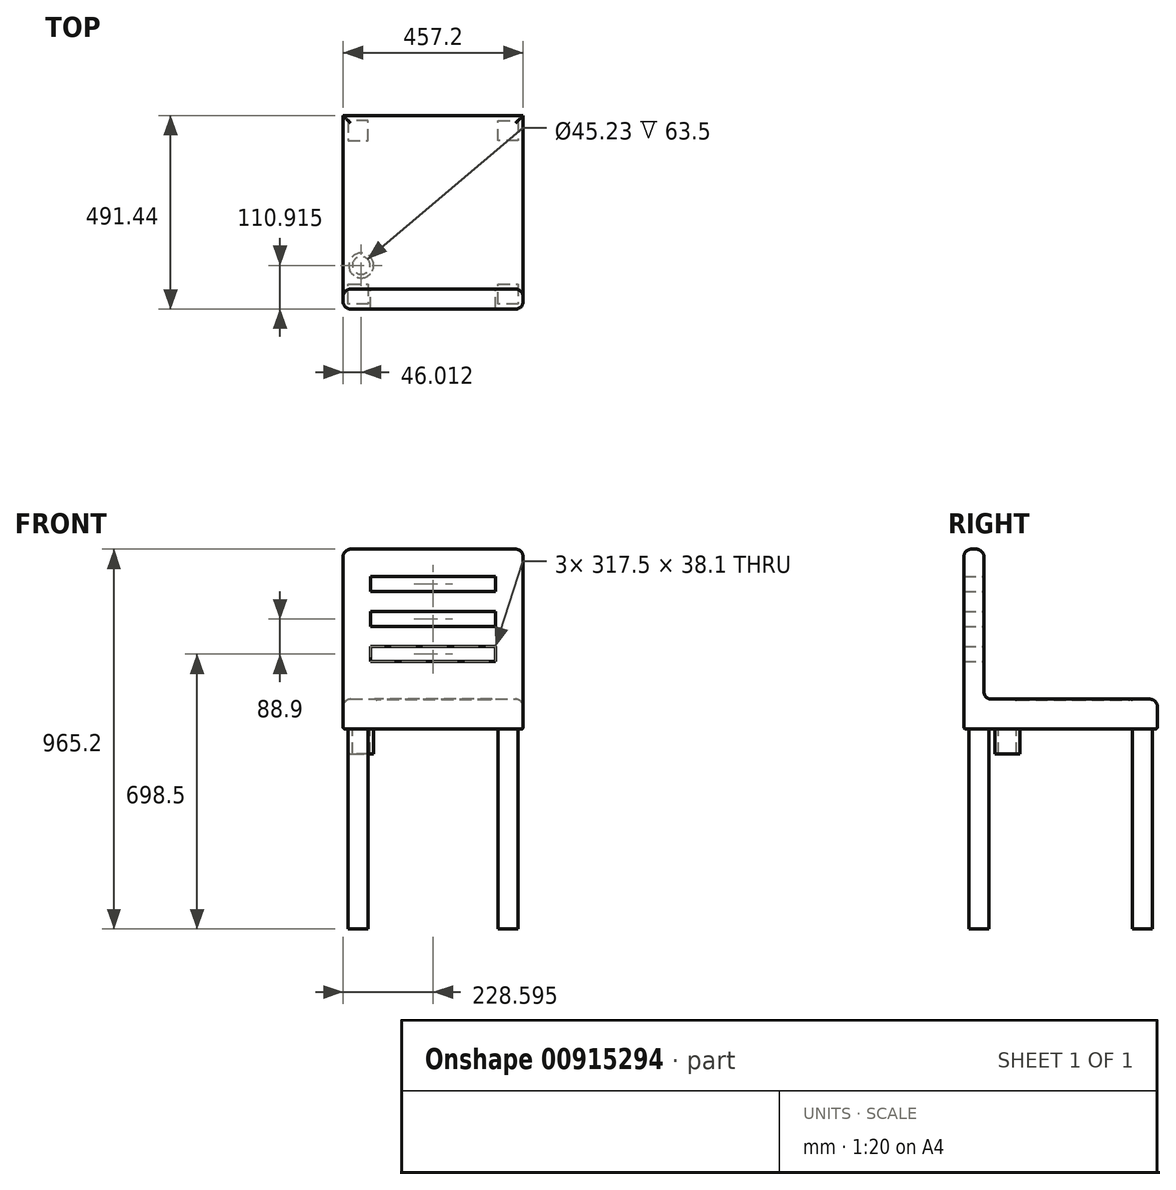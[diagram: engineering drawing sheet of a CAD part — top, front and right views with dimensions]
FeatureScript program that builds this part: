
annotation { "Feature Type Name" : "Feature", "Feature Type Description" : "" }
export const myFeature = defineFeature(function(context is Context, id is Id, definition is map)
    precondition{}
    {
        {
            var Q0;
            Q0=qCreatedBy(makeId("Top.planeOp"),FACE);
            var sketch = newSketch(context, id + "F0", { "sketchPlane" : qUnion([Q0])});
            skLineSegment(sketch, "E0.bottom", {"start": v(-229.23, 212.04) * mm, "end": v(227.97, 212.04) * mm});
            skLineSegment(sketch, "E0.top", {"start": v(-229.23, -245.16) * mm, "end": v(227.97, -245.16) * mm});
            skLineSegment(sketch, "E0.left", {"start": v(-229.23, 212.04) * mm, "end": v(-229.23, -245.16) * mm});
            skLineSegment(sketch, "E0.right", {"start": v(227.97, 212.04) * mm, "end": v(227.97, -245.16) * mm});
            skSolve(sketch);
        }
        {
            var Q0;
            Q0=qCreatedBy(makeId("Front.planeOp"),FACE);
            cPlane(context, id + "F1", {"entities" : qUnion([Q0]), "cplaneType" : CPlaneType.OFFSET, "offset" : 228.6 * mm, "width" : 152.4 * mm, "height" : 152.4 * mm});
        }
        {
            var Q0;
            Q0=qCreatedBy(id+"F1.planeOp",FACE);
            var sketch = newSketch(context, id + "F2", { "sketchPlane" : qUnion([Q0])});
            skLineSegment(sketch, "E1", {"start": v(-229.23, 0) * mm, "end": v(-229.23, 457.2) * mm});
            skLineSegment(sketch, "E2", {"start": v(-229.23, 457.2) * mm, "end": v(227.97, 457.2) * mm});
            skLineSegment(sketch, "E3", {"start": v(227.97, 457.2) * mm, "end": v(227.97, 0) * mm});
            skLineSegment(sketch, "E4", {"start": v(-229.23, 0) * mm, "end": v(227.97, 0) * mm});
            skSolve(sketch);
        }
        {
            var Q0;
            Q0=makeQuery(id+"F2.imprint","IMPRINT",FACE,{"disambiguationData":[TD([[makeQuery(id+"F2.imprint","IMPRINT",EDGE,{"derivedFrom":sQuery(id+"F2.wireOp",EDGE,"E1")}),-1.0]])]});
            extrude(context, id + "F3", {"entities" : qUnion([Q0]), "depth" : 50.8 * mm, "offsetDistance" : 25.4 * mm});
        }
        {
            var Q0;
            Q0=makeQuery(id+"F0.imprint","IMPRINT",FACE,{"disambiguationData":[TD([[makeQuery(id+"F0.imprint","IMPRINT",EDGE,{"derivedFrom":sQuery(id+"F0.wireOp",EDGE,"E0.bottom")}),-1.0]])]});
            extrude(context, id + "F4", {"entities" : qUnion([Q0]), "operationType" : NewBodyOperationType.ADD, "depth" : 76.2 * mm, "offsetDistance" : 25.4 * mm});
        }
        {
            var Q0;
            Q0=makeQuery(id+"F4.boolean.opBoolean","MERGE",FACE,{"derivedFrom":[makeQuery(id+"F3.opExtrude","SWEPT_FACE",FACE,{"disambiguationData":[OSD([sQuery(id+"F2.wireOp",EDGE,"E4")])]}),makeQuery(id+"F4.opExtrude","CAP_FACE",FACE,{"disambiguationData":[OSD([sQuery(id+"F0.wireOp",EDGE,"E0.bottom"),sQuery(id+"F0.wireOp",EDGE,"E0.top"),sQuery(id+"F0.wireOp",EDGE,"E0.left"),sQuery(id+"F0.wireOp",EDGE,"E0.right")])],"isStart":true})]});
            var sketch = newSketch(context, id + "F5", { "sketchPlane" : qUnion([Q0])});
            skLineSegment(sketch, "E5", {"start": v(-216.53, 266.7) * mm, "end": v(-216.53, 215.9) * mm});
            skLineSegment(sketch, "E6", {"start": v(-216.53, 215.9) * mm, "end": v(-165.73, 215.9) * mm});
            skLineSegment(sketch, "E7", {"start": v(-165.73, 215.9) * mm, "end": v(-165.73, 266.7) * mm});
            skLineSegment(sketch, "E8", {"start": v(-165.73, 266.7) * mm, "end": v(-216.53, 266.7) * mm});
            skLineSegment(sketch, "E9", {"start": v(215.27, 266.7) * mm, "end": v(164.47, 266.7) * mm});
            skLineSegment(sketch, "E10", {"start": v(164.47, 266.7) * mm, "end": v(164.47, 215.9) * mm});
            skLineSegment(sketch, "E11", {"start": v(164.47, 215.9) * mm, "end": v(215.27, 215.9) * mm});
            skLineSegment(sketch, "E12", {"start": v(215.27, 215.9) * mm, "end": v(215.27, 266.7) * mm});
            skLineSegment(sketch, "E13", {"start": v(164.47, -148.54) * mm, "end": v(164.47, -199.34) * mm});
            skLineSegment(sketch, "E14", {"start": v(164.47, -199.34) * mm, "end": v(215.27, -199.34) * mm});
            skLineSegment(sketch, "E15", {"start": v(215.27, -199.34) * mm, "end": v(215.27, -148.54) * mm});
            skLineSegment(sketch, "E16", {"start": v(215.27, -148.54) * mm, "end": v(164.47, -148.54) * mm});
            skLineSegment(sketch, "E17", {"start": v(-216.53, -199.34) * mm, "end": v(-216.53, -148.54) * mm});
            skLineSegment(sketch, "E18", {"start": v(-216.53, -148.54) * mm, "end": v(-165.73, -148.54) * mm});
            skLineSegment(sketch, "E19", {"start": v(-165.73, -148.54) * mm, "end": v(-165.73, -199.34) * mm});
            skLineSegment(sketch, "E20", {"start": v(-165.73, -199.34) * mm, "end": v(-216.53, -199.34) * mm});
            skSolve(sketch);
        }
        {
            var Q0;
            Q0 = qSketchRegion(id + "F5", true);
            var Q1;
            Q1 = qConstructionFilter(qBodyType(qCreatedBy(id + "F5" ,EDGE), BodyType.WIRE), ConstructionObject.NO);
            extrude(context, id + "F6", {"entities" : qUnion([Q0]), "operationType" : NewBodyOperationType.ADD, "surfaceOperationType" : NewSurfaceOperationType.ADD, "surfaceEntities" : qUnion([Q1]), "depth" : 508 * mm, "offsetDistance" : 25.4 * mm});
        }
        {
            var Q0;
            Q0=makeQuery(id+"F4.boolean.opBoolean","INTERSECT",EDGE,{"derivedFrom":[makeQuery(id+"F3.opExtrude","CAP_FACE",FACE,{"disambiguationData":[OSD([sQuery(id+"F2.wireOp",EDGE,"E1"),sQuery(id+"F2.wireOp",EDGE,"E2"),sQuery(id+"F2.wireOp",EDGE,"E3"),sQuery(id+"F2.wireOp",EDGE,"E4")])],"isStart":true}),makeQuery(id+"F4.opExtrude","CAP_FACE",FACE,{"disambiguationData":[OSD([sQuery(id+"F0.wireOp",EDGE,"E0.bottom"),sQuery(id+"F0.wireOp",EDGE,"E0.top"),sQuery(id+"F0.wireOp",EDGE,"E0.left"),sQuery(id+"F0.wireOp",EDGE,"E0.right")])],"isStart":false})]});
            var Q1;
            Q1=makeQuery(id+"F3.opExtrude","CAP_EDGE",EDGE,{"disambiguationData":[OSD([sQuery(id+"F2.wireOp",EDGE,"E2")])],"isStart":true});
            var Q2;
            Q2=makeQuery(id+"F3.opExtrude","CAP_EDGE",EDGE,{"disambiguationData":[OSD([sQuery(id+"F2.wireOp",EDGE,"E1")])],"isStart":true});
            var Q3;
            Q3=makeQuery(id+"F3.opExtrude","CAP_EDGE",EDGE,{"disambiguationData":[OSD([sQuery(id+"F2.wireOp",EDGE,"E3")])],"isStart":true});
            var Q4;
            Q4=makeQuery(id+"F3.opExtrude","CAP_EDGE",EDGE,{"disambiguationData":[OSD([sQuery(id+"F2.wireOp",EDGE,"E2")])],"isStart":false});
            var Q5;
            Q5=makeQuery(id+"F3.opExtrude","CAP_EDGE",EDGE,{"disambiguationData":[OSD([sQuery(id+"F2.wireOp",EDGE,"E3")])],"isStart":false});
            var Q6;
            Q6=makeQuery(id+"F3.opExtrude","SWEPT_EDGE",EDGE,{"disambiguationData":[OSD([sQuery(id+"F2.wireOp",EDGE,"E2"),sQuery(id+"F2.wireOp",EDGE,"E3")])]});
            var Q7;
            Q7=makeQuery(id+"F3.opExtrude","SWEPT_EDGE",EDGE,{"disambiguationData":[OSD([sQuery(id+"F2.wireOp",EDGE,"E1"),sQuery(id+"F2.wireOp",EDGE,"E2")])]});
            var Q8;
            Q8=makeQuery(id+"F4.opExtrude","CAP_EDGE",EDGE,{"disambiguationData":[OSD([sQuery(id+"F0.wireOp",EDGE,"E0.left")])],"isStart":false});
            var Q9;
            Q9=makeQuery(id+"F4.opExtrude","CAP_EDGE",EDGE,{"disambiguationData":[OSD([sQuery(id+"F0.wireOp",EDGE,"E0.right")])],"isStart":false});
            var Q10;
            Q10=makeQuery(id+"F4.opExtrude","CAP_EDGE",EDGE,{"disambiguationData":[OSD([sQuery(id+"F0.wireOp",EDGE,"E0.bottom")])],"isStart":false});
            var Q11;
            Q11=makeQuery(id+"F3.opExtrude","CAP_EDGE",EDGE,{"disambiguationData":[OSD([sQuery(id+"F2.wireOp",EDGE,"E1")])],"isStart":false});
            fillet(context, id + "F7", {"entities" : qUnion([Q0, Q1, Q2, Q3, Q4, Q5, Q6, Q7, Q8, Q9, Q10, Q11]), "radius" : 19.05 * mm, "tangentPropagation" : true, "allowEdgeOverflow" : false});
        }
        {
            var Q0;
            Q0=makeQuery(id+"F3.opExtrude","CAP_FACE",FACE,{"disambiguationData":[OSD([sQuery(id+"F2.wireOp",EDGE,"E1"),sQuery(id+"F2.wireOp",EDGE,"E2"),sQuery(id+"F2.wireOp",EDGE,"E3"),sQuery(id+"F2.wireOp",EDGE,"E4")])],"isStart":false});
            var sketch = newSketch(context, id + "F8", { "sketchPlane" : qUnion([Q0])});
            skLineSegment(sketch, "E21.bottom", {"start": v(-159.38, 387.35) * mm, "end": v(158.12, 387.35) * mm});
            skLineSegment(sketch, "E21.top", {"start": v(-159.38, 349.25) * mm, "end": v(158.12, 349.25) * mm});
            skLineSegment(sketch, "E21.left", {"start": v(-159.38, 387.35) * mm, "end": v(-159.38, 349.25) * mm});
            skLineSegment(sketch, "E21.right", {"start": v(158.12, 387.35) * mm, "end": v(158.12, 349.25) * mm});
            skLineSegment(sketch, "E22.bottom", {"start": v(158.12, 298.45) * mm, "end": v(-159.38, 298.45) * mm});
            skLineSegment(sketch, "E22.top", {"start": v(158.12, 260.35) * mm, "end": v(-159.38, 260.35) * mm});
            skLineSegment(sketch, "E22.left", {"start": v(158.12, 298.45) * mm, "end": v(158.12, 260.35) * mm});
            skLineSegment(sketch, "E22.right", {"start": v(-159.38, 298.45) * mm, "end": v(-159.38, 260.35) * mm});
            skLineSegment(sketch, "E23.bottom", {"start": v(-159.38, 209.55) * mm, "end": v(158.12, 209.55) * mm});
            skLineSegment(sketch, "E23.top", {"start": v(-159.38, 171.45) * mm, "end": v(158.12, 171.45) * mm});
            skLineSegment(sketch, "E23.left", {"start": v(-159.38, 209.55) * mm, "end": v(-159.38, 171.45) * mm});
            skLineSegment(sketch, "E23.right", {"start": v(158.12, 209.55) * mm, "end": v(158.12, 171.45) * mm});
            skSolve(sketch);
        }
        {
            var Q0;
            Q0 = qSketchRegion(id + "F8", true);
            extrude(context, id + "F9", {"entities" : qUnion([Q0]), "operationType" : NewBodyOperationType.REMOVE, "endBound" : BoundingType.SYMMETRIC, "depth" : 127 * mm, "offsetDistance" : 25.4 * mm});
        }
        {
            var Q0;
            Q0=makeQuery(id+"F4.boolean.opBoolean","MERGE",FACE,{"derivedFrom":[makeQuery(id+"F3.opExtrude","SWEPT_FACE",FACE,{"disambiguationData":[OSD([sQuery(id+"F2.wireOp",EDGE,"E4")])]}),makeQuery(id+"F4.opExtrude","CAP_FACE",FACE,{"disambiguationData":[OSD([sQuery(id+"F0.wireOp",EDGE,"E0.bottom"),sQuery(id+"F0.wireOp",EDGE,"E0.top"),sQuery(id+"F0.wireOp",EDGE,"E0.left"),sQuery(id+"F0.wireOp",EDGE,"E0.right")])],"isStart":true})]});
            var sketch = newSketch(context, id + "F10", { "sketchPlane" : qUnion([Q0])});
            skCircle(sketch, "E24", {"center": v(-183.22, 168.49) * mm, "radius": 22.62 * mm});
            skCircle(sketch, "E25", {"center": v(-183.22, 168.49) * mm, "radius": 31.73 * mm});
            skSolve(sketch);
        }
        {
            var Q0;
            Q0 = qSketchRegion(id + "F10", true);
            extrude(context, id + "F11", {"entities" : qUnion([Q0]), "operationType" : NewBodyOperationType.ADD, "depth" : 63.5 * mm, "offsetDistance" : 25.4 * mm});
        }
        {
            var Q0;
            Q0=makeQuery(id+"F4.opExtrude","CAP_FACE",FACE,{"disambiguationData":[OSD([sQuery(id+"F0.wireOp",EDGE,"E0.bottom"),sQuery(id+"F0.wireOp",EDGE,"E0.top"),sQuery(id+"F0.wireOp",EDGE,"E0.left"),sQuery(id+"F0.wireOp",EDGE,"E0.right")])],"isStart":false});
            var sketch = newSketch(context, id + "F12", { "sketchPlane" : qUnion([Q0])});
            skCircle(sketch, "E26", {"center": v(0, 0) * mm, "radius": 147.06 * mm});
            skSolve(sketch);
        }
        {
            var Q0;
            Q0=makeQuery(id+"F12.imprint","IMPRINT",FACE,{"disambiguationData":[TD([[makeQuery(id+"F12.imprint","IMPRINT",EDGE,{"derivedFrom":sQuery(id+"F12.wireOp",EDGE,"E26")}),1.0]])]});
            extrude(context, id + "F13", {"entities" : qUnion([Q0]), "operationType" : NewBodyOperationType.REMOVE, "oppositeDirection" : true, "depth" : 2.54 * mm, "offsetDistance" : 25.4 * mm});
        }
        {
            var Q0;
            Q0=makeQuery(id+"F13.boolean.opBoolean","COPY",EDGE,{"derivedFrom":makeQuery(id+"F13.opExtrude","CAP_EDGE",EDGE,{"disambiguationData":[OSD([sQuery(id+"F12.wireOp",EDGE,"E26")])],"isStart":false})});
            fillet(context, id + "F14", {"entities" : qUnion([Q0]), "radius" : 5.08 * mm, "tangentPropagation" : true, "allowEdgeOverflow" : false});
        }
        {
            var Q0;
            Q0=makeQuery(id+"F14.opFillet","BLEND_EDGE",EDGE,{"blendedFrom":[makeQuery(id+"F13.boolean.opBoolean","COPY",EDGE,{"derivedFrom":makeQuery(id+"F13.opExtrude","CAP_EDGE",EDGE,{"disambiguationData":[OSD([sQuery(id+"F12.wireOp",EDGE,"E26")])],"isStart":false})}),makeQuery(id+"F4.opExtrude","CAP_FACE",FACE,{"disambiguationData":[OSD([sQuery(id+"F0.wireOp",EDGE,"E0.bottom"),sQuery(id+"F0.wireOp",EDGE,"E0.top"),sQuery(id+"F0.wireOp",EDGE,"E0.left"),sQuery(id+"F0.wireOp",EDGE,"E0.right")])],"isStart":false})],"blendedInto":[makeQuery(id+"F4.opExtrude","CAP_FACE",FACE,{"disambiguationData":[OSD([sQuery(id+"F0.wireOp",EDGE,"E0.bottom"),sQuery(id+"F0.wireOp",EDGE,"E0.top"),sQuery(id+"F0.wireOp",EDGE,"E0.left"),sQuery(id+"F0.wireOp",EDGE,"E0.right")])],"isStart":false})]});
            fillet(context, id + "F15", {"entities" : qUnion([Q0]), "radius" : 5.08 * mm, "tangentPropagation" : true, "allowEdgeOverflow" : false});
        }
        {
            var Q0;
            Q0=makeQuery(id+"F4.boolean.opBoolean","MERGE",EDGE,{"derivedFrom":[makeQuery(id+"F3.opExtrude","SWEPT_EDGE",EDGE,{"disambiguationData":[OSD([sQuery(id+"F2.wireOp",EDGE,"E1"),sQuery(id+"F2.wireOp",EDGE,"E4")])]}),makeQuery(id+"F4.opExtrude","CAP_EDGE",EDGE,{"disambiguationData":[OSD([sQuery(id+"F0.wireOp",EDGE,"E0.left")])],"isStart":true})]});
            var Q1;
            Q1=makeQuery(id+"F4.opExtrude","CAP_EDGE",EDGE,{"disambiguationData":[OSD([sQuery(id+"F0.wireOp",EDGE,"E0.bottom")])],"isStart":true});
            var Q2;
            Q2=makeQuery(id+"F4.boolean.opBoolean","MERGE",EDGE,{"derivedFrom":[makeQuery(id+"F3.opExtrude","SWEPT_EDGE",EDGE,{"disambiguationData":[OSD([sQuery(id+"F2.wireOp",EDGE,"E3"),sQuery(id+"F2.wireOp",EDGE,"E4")])]}),makeQuery(id+"F4.opExtrude","CAP_EDGE",EDGE,{"disambiguationData":[OSD([sQuery(id+"F0.wireOp",EDGE,"E0.right")])],"isStart":true})]});
            var Q3;
            Q3=makeQuery(id+"F3.opExtrude","CAP_EDGE",EDGE,{"disambiguationData":[OSD([sQuery(id+"F2.wireOp",EDGE,"E4")])],"isStart":false});
            fillet(context, id + "F16", {"entities" : qUnion([Q0, Q1, Q2, Q3]), "radius" : 5.08 * mm, "tangentPropagation" : true, "allowEdgeOverflow" : false});
        }
    });
